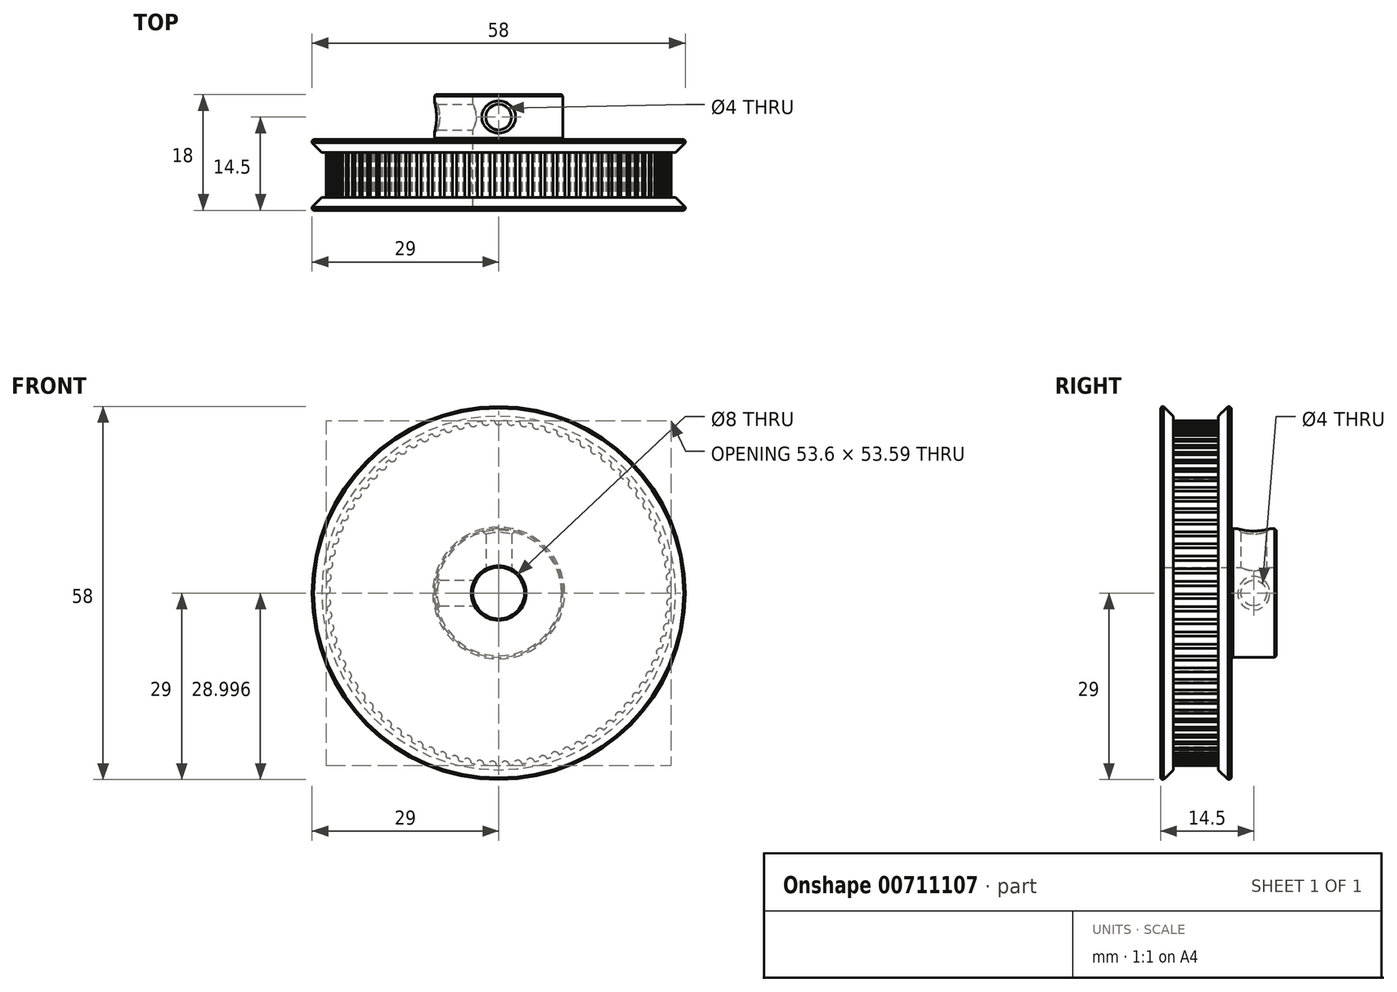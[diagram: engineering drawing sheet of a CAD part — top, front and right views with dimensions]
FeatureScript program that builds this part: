
annotation { "Feature Type Name" : "Feature", "Feature Type Description" : "" }
export const myFeature = defineFeature(function(context is Context, id is Id, definition is map)
    precondition{}
    {
        {
            var Q0;
            Q0=qCreatedBy(makeId("Front.planeOp"),FACE);
            var sketch = newSketch(context, id + "F0", { "sketchPlane" : qUnion([Q0])});
            skCircle(sketch, "E0", {"center": v(0, 0) * mm, "radius": 26.8 * mm});
            skSolve(sketch);
        }
        {
            var Q0;
            Q0 = qSketchRegion(id + "F0", true);
            extrude(context, id + "F1", {"entities" : qUnion([Q0]), "endBound" : BoundingType.SYMMETRIC, "depth" : 7 * mm, "offsetDistance" : 25 * mm});
        }
        {
            var Q0;
            Q0=makeQuery(id+"F1.opExtrude","CAP_FACE",FACE,{"disambiguationData":[OSD([sQuery(id+"F0.wireOp",EDGE,"E0")])],"isStart":false});
            var sketch = newSketch(context, id + "F2", { "sketchPlane" : qUnion([Q0])});
            skCircle(sketch, "E1", {"center": v(0, 0) * mm, "radius": 29 * mm});
            skSolve(sketch);
        }
        {
            var Q0;
            Q0 = qSketchRegion(id + "F2", true);
            extrude(context, id + "F3", {"entities" : qUnion([Q0]), "operationType" : NewBodyOperationType.ADD, "depth" : 2 * mm, "offsetDistance" : 25 * mm});
        }
        {
            var Q0;
            Q0=makeQuery(id+"F1.opExtrude","CAP_FACE",FACE,{"disambiguationData":[OSD([sQuery(id+"F0.wireOp",EDGE,"E0")])],"isStart":true});
            var sketch = newSketch(context, id + "F4", { "sketchPlane" : qUnion([Q0])});
            skCircle(sketch, "E2", {"center": v(0, 0) * mm, "radius": 29 * mm});
            skSolve(sketch);
        }
        {
            var Q0;
            Q0 = qSketchRegion(id + "F4", true);
            extrude(context, id + "F5", {"entities" : qUnion([Q0]), "operationType" : NewBodyOperationType.ADD, "depth" : 2 * mm, "offsetDistance" : 25 * mm});
        }
        {
            var Q0;
            Q0=makeQuery(id+"F5.opExtrude","CAP_FACE",FACE,{"disambiguationData":[OSD([sQuery(id+"F4.wireOp",EDGE,"E2")])],"isStart":false});
            var sketch = newSketch(context, id + "F6", { "sketchPlane" : qUnion([Q0])});
            skCircle(sketch, "E3", {"center": v(0, 0) * mm, "radius": 10 * mm});
            skSolve(sketch);
        }
        {
            var Q0;
            Q0 = qSketchRegion(id + "F6", true);
            extrude(context, id + "F7", {"entities" : qUnion([Q0]), "operationType" : NewBodyOperationType.ADD, "depth" : 7 * mm, "offsetDistance" : 25 * mm});
        }
        {
            var Q0;
            Q0=makeQuery(id+"F7.opExtrude","CAP_FACE",FACE,{"disambiguationData":[OSD([sQuery(id+"F6.wireOp",EDGE,"E3")])],"isStart":false});
            var sketch = newSketch(context, id + "F8", { "sketchPlane" : qUnion([Q0])});
            skCircle(sketch, "E4", {"center": v(0, 0) * mm, "radius": 4 * mm});
            skSolve(sketch);
        }
        {
            var Q0;
            Q0 = qSketchRegion(id + "F8", true);
            extrude(context, id + "F9", {"entities" : qUnion([Q0]), "operationType" : NewBodyOperationType.REMOVE, "endBound" : BoundingType.THROUGH_ALL, "oppositeDirection" : true, "depth" : 25 * mm, "offsetDistance" : 25 * mm});
        }
        {
            var Q0;
            Q0=makeQuery(id+"F3.opExtrude","CAP_FACE",FACE,{"disambiguationData":[OSD([sQuery(id+"F2.wireOp",EDGE,"E1")])],"isStart":true});
            var sketch = newSketch(context, id + "F10", { "sketchPlane" : qUnion([Q0])});
            skCircle(sketch, "E5", {"center": v(0, 0) * mm, "radius": 26.8 * mm, "construction": true});
            skLineSegment(sketch, "E6", {"start": v(0, 0) * mm, "end": v(0, 26.8) * mm, "construction": true});
            skCircle(sketch, "E7", {"center": v(0, 26.8) * mm, "radius": 0.65 * mm});
            skCircle(sketch, "E8.1.0", {"center": v(-1.98, 26.73) * mm, "radius": 0.65 * mm});
            skCircle(sketch, "E8.2.0", {"center": v(-3.95, 26.5) * mm, "radius": 0.65 * mm});
            skCircle(sketch, "E8.3.0", {"center": v(-5.9, 26.14) * mm, "radius": 0.65 * mm});
            skCircle(sketch, "E8.4.0", {"center": v(-7.8, 25.64) * mm, "radius": 0.65 * mm});
            skCircle(sketch, "E8.5.0", {"center": v(-9.68, 25) * mm, "radius": 0.65 * mm});
            skCircle(sketch, "E8.6.0", {"center": v(-11.5, 24.2) * mm, "radius": 0.65 * mm});
            skCircle(sketch, "E8.7.0", {"center": v(-13.26, 23.3) * mm, "radius": 0.65 * mm});
            skCircle(sketch, "E8.8.0", {"center": v(-14.94, 22.25) * mm, "radius": 0.65 * mm});
            skCircle(sketch, "E8.9.0", {"center": v(-16.54, 21.08) * mm, "radius": 0.65 * mm});
            skCircle(sketch, "E8.10.0", {"center": v(-18.06, 19.8) * mm, "radius": 0.65 * mm});
            skCircle(sketch, "E8.11.0", {"center": v(-19.47, 18.42) * mm, "radius": 0.65 * mm});
            skCircle(sketch, "E8.12.0", {"center": v(-20.78, 16.93) * mm, "radius": 0.65 * mm});
            skCircle(sketch, "E8.13.0", {"center": v(-21.97, 15.35) * mm, "radius": 0.65 * mm});
            skCircle(sketch, "E8.14.0", {"center": v(-23.04, 13.68) * mm, "radius": 0.65 * mm});
            skCircle(sketch, "E8.15.0", {"center": v(-24, 11.95) * mm, "radius": 0.65 * mm});
            skCircle(sketch, "E8.16.0", {"center": v(-24.8, 10.14) * mm, "radius": 0.65 * mm});
            skCircle(sketch, "E8.17.0", {"center": v(-25.49, 8.28) * mm, "radius": 0.65 * mm});
            skCircle(sketch, "E8.18.0", {"center": v(-26.03, 6.38) * mm, "radius": 0.65 * mm});
            skCircle(sketch, "E8.19.0", {"center": v(-26.43, 4.44) * mm, "radius": 0.65 * mm});
            skCircle(sketch, "E8.20.0", {"center": v(-26.69, 2.47) * mm, "radius": 0.65 * mm});
            skCircle(sketch, "E8.21.0", {"center": v(-26.8, 0.5) * mm, "radius": 0.65 * mm});
            skCircle(sketch, "E8.22.0", {"center": v(-26.76, -1.49) * mm, "radius": 0.65 * mm});
            skCircle(sketch, "E8.23.0", {"center": v(-26.58, -3.46) * mm, "radius": 0.65 * mm});
            skCircle(sketch, "E8.24.0", {"center": v(-26.25, -5.41) * mm, "radius": 0.65 * mm});
            skCircle(sketch, "E8.25.0", {"center": v(-25.78, -7.33) * mm, "radius": 0.65 * mm});
            skCircle(sketch, "E8.26.0", {"center": v(-25.16, -9.22) * mm, "radius": 0.65 * mm});
            skCircle(sketch, "E8.27.0", {"center": v(-24.42, -11.05) * mm, "radius": 0.65 * mm});
            skCircle(sketch, "E8.28.0", {"center": v(-23.53, -12.82) * mm, "radius": 0.65 * mm});
            skCircle(sketch, "E8.29.0", {"center": v(-22.52, -14.53) * mm, "radius": 0.65 * mm});
            skCircle(sketch, "E8.30.0", {"center": v(-21.39, -16.15) * mm, "radius": 0.65 * mm});
            skCircle(sketch, "E8.31.0", {"center": v(-20.14, -17.69) * mm, "radius": 0.65 * mm});
            skCircle(sketch, "E8.32.0", {"center": v(-18.77, -19.12) * mm, "radius": 0.65 * mm});
            skCircle(sketch, "E8.33.0", {"center": v(-17.31, -20.46) * mm, "radius": 0.65 * mm});
            skCircle(sketch, "E8.34.0", {"center": v(-15.75, -21.68) * mm, "radius": 0.65 * mm});
            skCircle(sketch, "E8.35.0", {"center": v(-14.1, -22.79) * mm, "radius": 0.65 * mm});
            skCircle(sketch, "E8.36.0", {"center": v(-12.39, -23.77) * mm, "radius": 0.65 * mm});
            skCircle(sketch, "E8.37.0", {"center": v(-10.6, -24.62) * mm, "radius": 0.65 * mm});
            skCircle(sketch, "E8.38.0", {"center": v(-8.75, -25.33) * mm, "radius": 0.65 * mm});
            skCircle(sketch, "E8.39.0", {"center": v(-6.86, -25.9) * mm, "radius": 0.65 * mm});
            skCircle(sketch, "E8.40.0", {"center": v(-4.92, -26.34) * mm, "radius": 0.65 * mm});
            skCircle(sketch, "E8.41.0", {"center": v(-2.97, -26.64) * mm, "radius": 0.65 * mm});
            skCircle(sketch, "E8.42.0", {"center": v(-1, -26.78) * mm, "radius": 0.65 * mm});
            skCircle(sketch, "E8.43.0", {"center": v(1, -26.78) * mm, "radius": 0.65 * mm});
            skCircle(sketch, "E8.44.0", {"center": v(2.97, -26.64) * mm, "radius": 0.65 * mm});
            skCircle(sketch, "E8.45.0", {"center": v(4.92, -26.34) * mm, "radius": 0.65 * mm});
            skCircle(sketch, "E8.46.0", {"center": v(6.86, -25.9) * mm, "radius": 0.65 * mm});
            skCircle(sketch, "E8.47.0", {"center": v(8.75, -25.33) * mm, "radius": 0.65 * mm});
            skCircle(sketch, "E8.48.0", {"center": v(10.6, -24.62) * mm, "radius": 0.65 * mm});
            skCircle(sketch, "E8.49.0", {"center": v(12.39, -23.77) * mm, "radius": 0.65 * mm});
            skCircle(sketch, "E8.50.0", {"center": v(14.1, -22.79) * mm, "radius": 0.65 * mm});
            skCircle(sketch, "E8.51.0", {"center": v(15.75, -21.68) * mm, "radius": 0.65 * mm});
            skCircle(sketch, "E8.52.0", {"center": v(17.31, -20.46) * mm, "radius": 0.65 * mm});
            skCircle(sketch, "E8.53.0", {"center": v(18.77, -19.12) * mm, "radius": 0.65 * mm});
            skCircle(sketch, "E8.54.0", {"center": v(20.14, -17.69) * mm, "radius": 0.65 * mm});
            skCircle(sketch, "E8.55.0", {"center": v(21.39, -16.15) * mm, "radius": 0.65 * mm});
            skCircle(sketch, "E8.56.0", {"center": v(22.52, -14.53) * mm, "radius": 0.65 * mm});
            skCircle(sketch, "E8.57.0", {"center": v(23.53, -12.82) * mm, "radius": 0.65 * mm});
            skCircle(sketch, "E8.58.0", {"center": v(24.42, -11.05) * mm, "radius": 0.65 * mm});
            skCircle(sketch, "E8.59.0", {"center": v(25.16, -9.22) * mm, "radius": 0.65 * mm});
            skCircle(sketch, "E8.60.0", {"center": v(25.78, -7.33) * mm, "radius": 0.65 * mm});
            skCircle(sketch, "E8.61.0", {"center": v(26.25, -5.41) * mm, "radius": 0.65 * mm});
            skCircle(sketch, "E8.62.0", {"center": v(26.58, -3.46) * mm, "radius": 0.65 * mm});
            skCircle(sketch, "E8.63.0", {"center": v(26.76, -1.49) * mm, "radius": 0.65 * mm});
            skCircle(sketch, "E8.64.0", {"center": v(26.8, 0.5) * mm, "radius": 0.65 * mm});
            skCircle(sketch, "E8.65.0", {"center": v(26.69, 2.47) * mm, "radius": 0.65 * mm});
            skCircle(sketch, "E8.66.0", {"center": v(26.43, 4.44) * mm, "radius": 0.65 * mm});
            skCircle(sketch, "E8.67.0", {"center": v(26.03, 6.38) * mm, "radius": 0.65 * mm});
            skCircle(sketch, "E8.68.0", {"center": v(25.49, 8.28) * mm, "radius": 0.65 * mm});
            skCircle(sketch, "E8.69.0", {"center": v(24.8, 10.14) * mm, "radius": 0.65 * mm});
            skCircle(sketch, "E8.70.0", {"center": v(24, 11.95) * mm, "radius": 0.65 * mm});
            skCircle(sketch, "E8.71.0", {"center": v(23.04, 13.68) * mm, "radius": 0.65 * mm});
            skCircle(sketch, "E8.72.0", {"center": v(21.97, 15.35) * mm, "radius": 0.65 * mm});
            skCircle(sketch, "E8.73.0", {"center": v(20.78, 16.93) * mm, "radius": 0.65 * mm});
            skCircle(sketch, "E8.74.0", {"center": v(19.47, 18.42) * mm, "radius": 0.65 * mm});
            skCircle(sketch, "E8.75.0", {"center": v(18.06, 19.8) * mm, "radius": 0.65 * mm});
            skCircle(sketch, "E8.76.0", {"center": v(16.54, 21.08) * mm, "radius": 0.65 * mm});
            skCircle(sketch, "E8.77.0", {"center": v(14.94, 22.25) * mm, "radius": 0.65 * mm});
            skCircle(sketch, "E8.78.0", {"center": v(13.26, 23.3) * mm, "radius": 0.65 * mm});
            skCircle(sketch, "E8.79.0", {"center": v(11.5, 24.2) * mm, "radius": 0.65 * mm});
            skCircle(sketch, "E8.80.0", {"center": v(9.68, 25) * mm, "radius": 0.65 * mm});
            skCircle(sketch, "E8.81.0", {"center": v(7.8, 25.64) * mm, "radius": 0.65 * mm});
            skCircle(sketch, "E8.82.0", {"center": v(5.9, 26.14) * mm, "radius": 0.65 * mm});
            skCircle(sketch, "E8.83.0", {"center": v(3.95, 26.5) * mm, "radius": 0.65 * mm});
            skCircle(sketch, "E8.84.0", {"center": v(1.98, 26.73) * mm, "radius": 0.65 * mm});
            skSolve(sketch);
        }
        {
            var Q0;
            Q0 = qSketchRegion(id + "F10", true);
            extrude(context, id + "F11", {"entities" : qUnion([Q0]), "operationType" : NewBodyOperationType.REMOVE, "depth" : 7 * mm, "offsetDistance" : 25 * mm});
        }
        {
            var Q0;
            Q0=makeQuery(id+"F3.opExtrude","CAP_EDGE",EDGE,{"disambiguationData":[OSD([sQuery(id+"F2.wireOp",EDGE,"E1")])],"isStart":true});
            var Q1;
            Q1=makeQuery(id+"F5.opExtrude","CAP_EDGE",EDGE,{"disambiguationData":[OSD([sQuery(id+"F4.wireOp",EDGE,"E2")])],"isStart":true});
            chamfer(context, id + "F12", {"entities" : qUnion([Q0, Q1]), "width" : 1.5 * mm, "tangentPropagation" : true});
        }
        {
            var Q0;
            Q0=qCreatedBy(makeId("Top.planeOp"),FACE);
            var sketch = newSketch(context, id + "F13", { "sketchPlane" : qUnion([Q0])});
            skLineSegment(sketch, "E9", {"start": v(0, 0) * mm, "end": v(0, 12.5) * mm, "construction": true});
            skCircle(sketch, "E10", {"center": v(0, 9) * mm, "radius": 2 * mm});
            skSolve(sketch);
        }
        {
            var Q0;
            Q0 = qSketchRegion(id + "F13", true);
            extrude(context, id + "F14", {"entities" : qUnion([Q0]), "operationType" : NewBodyOperationType.REMOVE, "endBound" : BoundingType.THROUGH_ALL, "depth" : 25 * mm, "offsetDistance" : 25 * mm});
        }
        {
            var Q0;
            Q0=qCreatedBy(makeId("Right.planeOp"),FACE);
            var sketch = newSketch(context, id + "F15", { "sketchPlane" : qUnion([Q0])});
            skLineSegment(sketch, "E11", {"start": v(0, 0) * mm, "end": v(12.5, 0) * mm, "construction": true});
            skCircle(sketch, "E12", {"center": v(9, 0) * mm, "radius": 2 * mm});
            skSolve(sketch);
        }
        {
            var Q0;
            Q0 = qSketchRegion(id + "F15", true);
            extrude(context, id + "F16", {"entities" : qUnion([Q0]), "operationType" : NewBodyOperationType.REMOVE, "endBound" : BoundingType.THROUGH_ALL, "oppositeDirection" : true, "depth" : 25 * mm, "offsetDistance" : 25 * mm});
        }
        {
            var Q0;
            Q0=makeQuery(id+"F14.boolean.opBoolean","INTERSECT",EDGE,{"derivedFrom":[makeQuery(id+"F7.opExtrude","SWEPT_FACE",FACE,{"disambiguationData":[OSD([sQuery(id+"F6.wireOp",EDGE,"E3")])]}),makeQuery(id+"F14.opExtrude","SWEPT_FACE",FACE,{"disambiguationData":[OSD([sQuery(id+"F13.wireOp",EDGE,"E10")])]})]});
            var Q1;
            Q1=makeQuery(id+"F16.boolean.opBoolean","INTERSECT",EDGE,{"derivedFrom":[makeQuery(id+"F7.opExtrude","SWEPT_FACE",FACE,{"disambiguationData":[OSD([sQuery(id+"F6.wireOp",EDGE,"E3")])]}),makeQuery(id+"F16.opExtrude","SWEPT_FACE",FACE,{"disambiguationData":[OSD([sQuery(id+"F15.wireOp",EDGE,"E12")])]})]});
            chamfer(context, id + "F17", {"entities" : qUnion([Q0, Q1]), "width" : 0.5 * mm, "tangentPropagation" : true});
        }
        {
            var Q0;
            Q0=makeQuery(id+"F7.opExtrude","CAP_FACE",FACE,{"disambiguationData":[OSD([sQuery(id+"F6.wireOp",EDGE,"E3")])],"isStart":false});
            var Q1;
            Q1=makeQuery(id+"F7.opExtrude","CAP_EDGE",EDGE,{"disambiguationData":[OSD([sQuery(id+"F6.wireOp",EDGE,"E3")])],"isStart":true});
            var Q2;
            Q2=makeQuery(id+"F5.opExtrude","CAP_FACE",FACE,{"disambiguationData":[OSD([sQuery(id+"F4.wireOp",EDGE,"E2")])],"isStart":false});
            var Q3;
            Q3=makeQuery(id+"F3.opExtrude","CAP_FACE",FACE,{"disambiguationData":[OSD([sQuery(id+"F2.wireOp",EDGE,"E1")])],"isStart":false});
            chamfer(context, id + "F18", {"entities" : qUnion([Q0, Q1, Q2, Q3]), "width" : 0.25 * mm, "tangentPropagation" : true});
        }
    });
